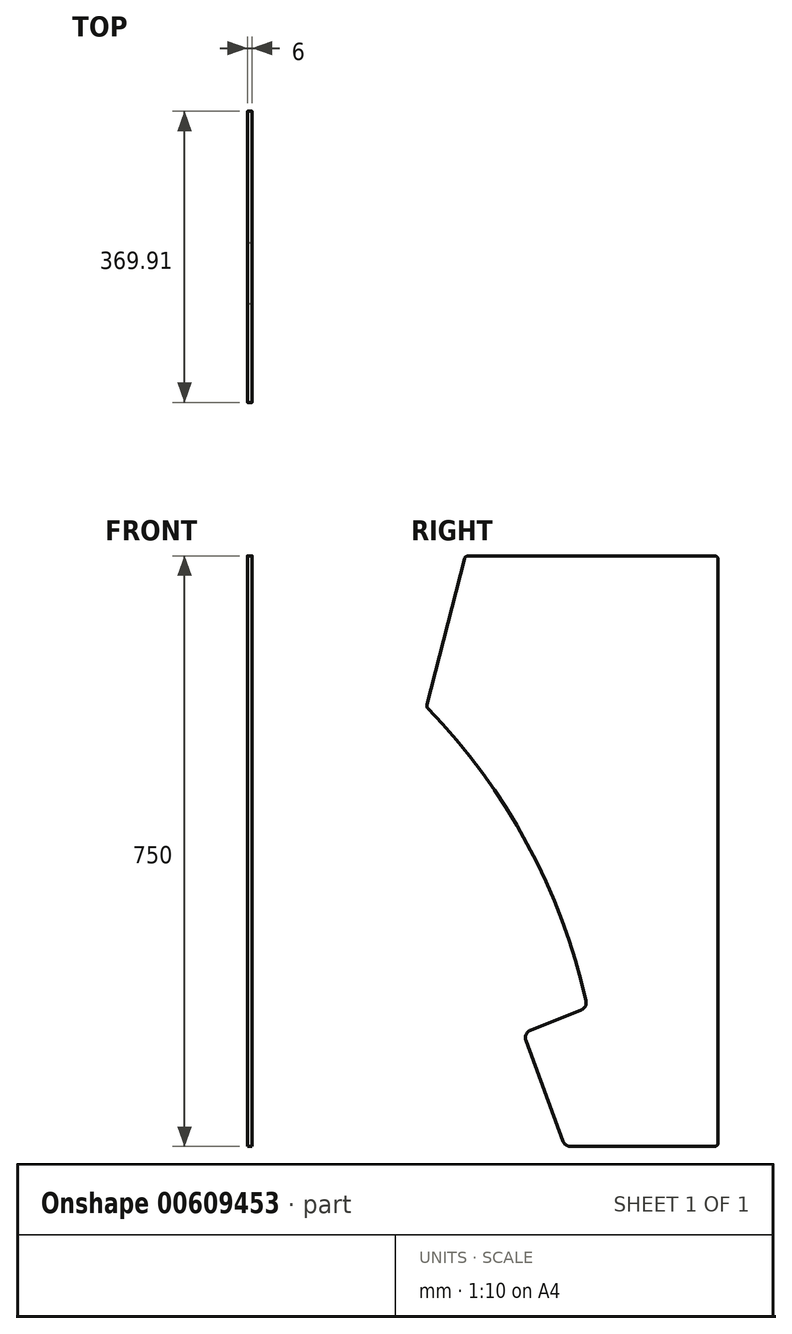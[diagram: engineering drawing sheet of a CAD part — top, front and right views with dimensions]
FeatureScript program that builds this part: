
annotation { "Feature Type Name" : "Feature", "Feature Type Description" : "" }
export const myFeature = defineFeature(function(context is Context, id is Id, definition is map)
    precondition{}
    {
        {
            var Q0;
            Q0=qCreatedBy(makeId("Right.planeOp"),FACE);
            var sketch = newSketch(context, id + "F0", { "sketchPlane" : qUnion([Q0])});
            skLineSegment(sketch, "E0", {"start": v(206.18, 379.01) * mm, "end": v(-115.06, 379.01) * mm});
            skLineSegment(sketch, "E1", {"start": v(206.18, 379.01) * mm, "end": v(206.18, -370.99) * mm});
            skLineSegment(sketch, "E2", {"start": v(206.18, -370.99) * mm, "end": v(11.88, -370.99) * mm});
            skLineSegment(sketch, "E3", {"start": v(11.88, -370.99) * mm, "end": v(-41.23, -227.2) * mm});
            skLineSegment(sketch, "E4", {"start": v(-115.06, 379.01) * mm, "end": v(-164.28, 187.3) * mm});
            skLineSegment(sketch, "E5", {"start": v(-41.23, -227.2) * mm, "end": v(40.38, -194.82) * mm});
            skArc(sketch, "E6", {"start": v(40.38, -194.82) * mm, "mid": v(-34.83, 10.77) * mm, "end": v(-164.28, 187.3) * mm});
            skSolve(sketch);
        }
        {
            var Q0;
            Q0=makeQuery(id+"F0.imprint","IMPRINT",FACE,{"disambiguationData":[TD([[makeQuery(id+"F0.imprint","IMPRINT",EDGE,{"derivedFrom":sQuery(id+"F0.wireOp",EDGE,"E0")}),1.0]])]});
            extrude(context, id + "F1", {"entities" : qUnion([Q0]), "depth" : 6 * mm, "offsetDistance" : 25.4 * mm});
        }
        {
            var Q0;
            Q0=makeQuery(id+"F1.opExtrude","SWEPT_EDGE",EDGE,{"disambiguationData":[OSD([sQuery(id+"F0.wireOp",EDGE,"E3"),sQuery(id+"F0.wireOp",EDGE,"E5")])]});
            fillet(context, id + "F2", {"entities" : qUnion([Q0]), "radius" : 10 * mm, "tangentPropagation" : true, "allowEdgeOverflow" : false});
        }
        {
            var Q0;
            Q0=makeQuery(id+"F1.opExtrude","SWEPT_EDGE",EDGE,{"disambiguationData":[OSD([sQuery(id+"F0.wireOp",EDGE,"E5"),sQuery(id+"F0.wireOp",EDGE,"E6")])]});
            fillet(context, id + "F3", {"entities" : qUnion([Q0]), "radius" : 10 * mm, "tangentPropagation" : true, "allowEdgeOverflow" : false});
        }
        {
            var Q0;
            Q0=makeQuery(id+"F1.opExtrude","SWEPT_EDGE",EDGE,{"disambiguationData":[OSD([sQuery(id+"F0.wireOp",EDGE,"E2"),sQuery(id+"F0.wireOp",EDGE,"E3")])]});
            fillet(context, id + "F4", {"entities" : qUnion([Q0]), "radius" : 10 * mm, "tangentPropagation" : true, "allowEdgeOverflow" : false});
        }
        {
            var Q0;
            Q0=makeQuery(id+"F1.opExtrude","SWEPT_EDGE",EDGE,{"disambiguationData":[OSD([sQuery(id+"F0.wireOp",EDGE,"E1"),sQuery(id+"F0.wireOp",EDGE,"E2")])]});
            fillet(context, id + "F5", {"entities" : qUnion([Q0]), "radius" : 4 * mm, "tangentPropagation" : true, "allowEdgeOverflow" : false});
        }
        {
            var Q0;
            Q0=makeQuery(id+"F1.opExtrude","SWEPT_EDGE",EDGE,{"disambiguationData":[OSD([sQuery(id+"F0.wireOp",EDGE,"E0"),sQuery(id+"F0.wireOp",EDGE,"E1")])]});
            fillet(context, id + "F6", {"entities" : qUnion([Q0]), "radius" : 4 * mm, "tangentPropagation" : true, "allowEdgeOverflow" : false});
        }
        {
            var Q0;
            Q0=makeQuery(id+"F1.opExtrude","SWEPT_EDGE",EDGE,{"disambiguationData":[OSD([sQuery(id+"F0.wireOp",EDGE,"E4"),sQuery(id+"F0.wireOp",EDGE,"E6")])]});
            fillet(context, id + "F7", {"entities" : qUnion([Q0]), "radius" : 5.08 * mm, "tangentPropagation" : true, "allowEdgeOverflow" : false});
        }
        {
            var Q0;
            Q0=makeQuery(id+"F1.opExtrude","SWEPT_EDGE",EDGE,{"disambiguationData":[OSD([sQuery(id+"F0.wireOp",EDGE,"E0"),sQuery(id+"F0.wireOp",EDGE,"E4")])]});
            fillet(context, id + "F8", {"entities" : qUnion([Q0]), "radius" : 5.08 * mm, "tangentPropagation" : true, "allowEdgeOverflow" : false});
        }
    });
